# Revit family: Bath-Whirlpool-Drop_In-STERLING-Heater-Lawson-76301100-H
name_source: partatom
category: Plumbing Fixtures
revit_build: Autodesk Revit 2015 (Build: 20140606_1530(x64)
units: mm (PartAtom-declared; Revit-internal decimal feet)

## types (2) — shared parameters
ADA = No
Apparent Load = 1800 VA
Assembly Code = D2010500
CW Connection = No
Cold Water Inlet = Cold Water Inlet
Date Modified = 11/06/2017
Default Elevation = 0"
Description = Lawson, Series 7630, 72inch x 36inch Whirlpool Bath with Heater
Electrical Connector = Yes
Electrical Note Heater = One dedicated circuits required, protected with Class A Ground-Fault Circuit-Interrupter (GFCI) or Residual Current Device (RCD)
Electrical Note Pump = One dedicated circuits required, protected with Class A Ground-Fault Circuit-Interrupter (GFCI) or Residual Current Device (RCD)
HW Connection = No
Height = 20 5/16"
Hot Water Inlet = Hot Water Inlet
Length = 72"
Manufacturer = STERLING Co.
MasterFormat 1995 = 15410
MasterFormat 2004 = 22.41.19
Material = Vikrell
Product Documentation Link = https://www.sterlingplumbing.com
Product Name = Lawson
Product Page URL = http://www.sterlingplumbing.com
URL = https://www.sterlingplumbing.com
Vent Connection = No
Voltage = 120 V
Waste Connection = Yes
Waste Water Outlet = Waste Water Outlet
Width = 36"

## per-type parameters (varying)
| type | Finish | Model | Type |
| 0-White | Kohler-Vikrell-0-White | 76301100-H-0 | 1 |
| 96-Biscuit | Kohler-Vikrell-96-Biscuit | 76301100-H-96 | 2 |

## geometry (parser evidence)
native form markers: Sweep x6
no freeform markers — native parametric forms only
